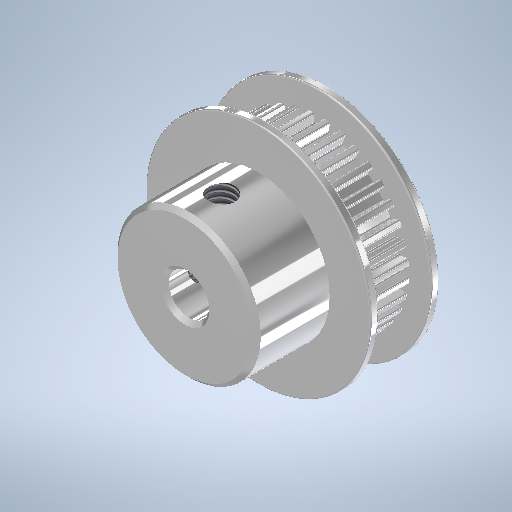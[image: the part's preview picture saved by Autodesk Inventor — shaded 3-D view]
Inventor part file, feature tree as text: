
AUTODESK INVENTOR PART (.ipt)
format: ipt  version: 2025.2 (Build 292293000, 293)  size: 628,224 bytes
history: native  units: mm
features: sketch x3, chamfer x2, pattern_circular x2, revolve x1, hole x1, extrude x1, fillet x1, other x1
ambient origin geometry x8: Origin, YZ Plane, XZ Plane, XY Plane, X Axis, Y Axis, Z Axis, Center Point
bodies: Solido1 (feature_tree)
feature tree (12):
  revolve  "Rivoluzione1"
  chamfer  "Smusso1"  Distance=5.0mm
  chamfer  "Smusso2"  Distance=17.7mm
  hole  "Foro1"  [1 undecoded]
  pattern_circular  "Serie circolare1"  [2 undecoded]
  extrude  "Estrusione1"  Depth=6.5mm
  pattern_circular  "Serie circolare2"  [2 undecoded]
  fillet  "Raccordo4"  Radius=22.4mm
  sketch  "Schizzo1"
  sketch  "Schizzo2"
  sketch  "Schizzo3"
  other  "Linea chiusa proiettata1"
note: 5 required parameter values undecoded (feature->parameter linkage not recoverable at this tier; creation-order binding heuristic only, values carry confidence <= 0.55)
